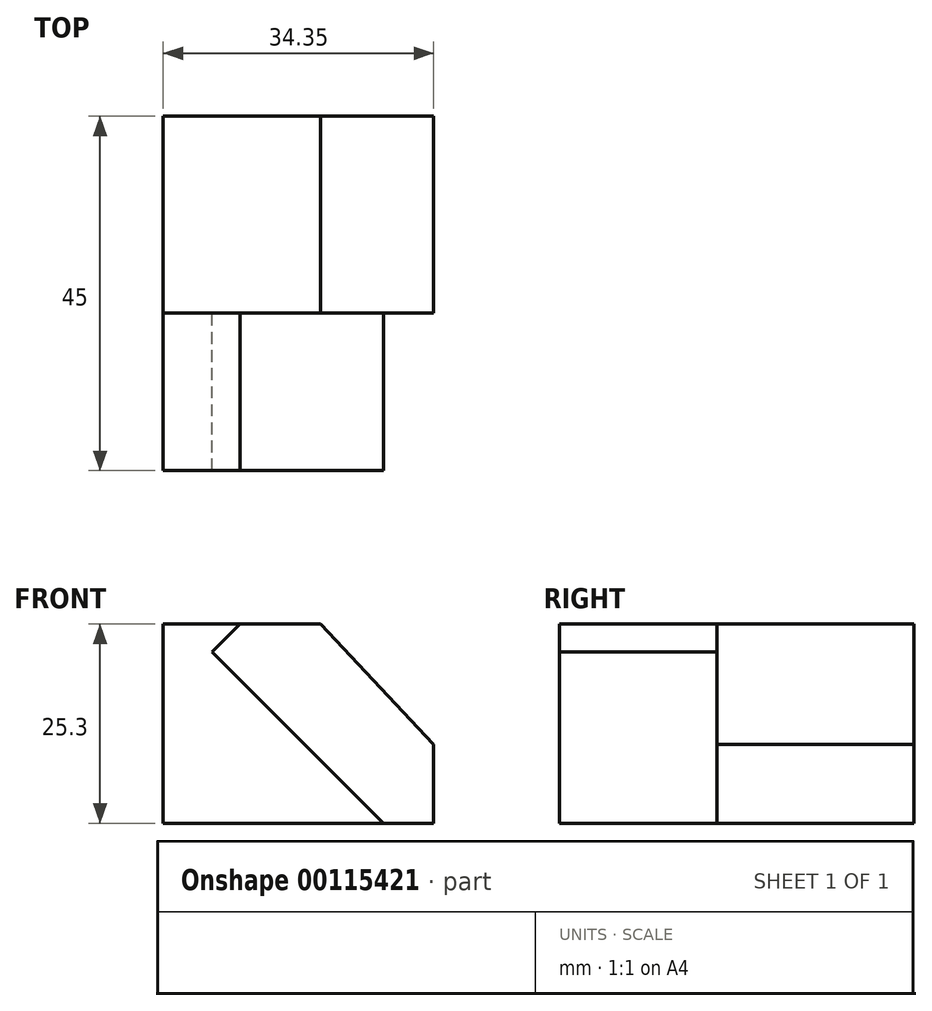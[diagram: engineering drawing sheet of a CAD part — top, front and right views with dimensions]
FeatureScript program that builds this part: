
annotation { "Feature Type Name" : "Feature", "Feature Type Description" : "" }
export const myFeature = defineFeature(function(context is Context, id is Id, definition is map)
    precondition{}
    {
        {
            var Q0;
            Q0=qCreatedBy(makeId("Front.planeOp"),FACE);
            var sketch = newSketch(context, id + "F0", { "sketchPlane" : qUnion([Q0])});
            skLineSegment(sketch, "E0", {"start": v(0, -6.35) * mm, "end": v(-28.11, 21.76) * mm, "construction": true});
            skLineSegment(sketch, "E1", {"start": v(0, 0) * mm, "end": v(-47.03, 0) * mm, "construction": true});
            skLineSegment(sketch, "E2", {"start": v(-6.35, 0) * mm, "end": v(-28.11, 21.76) * mm});
            skLineSegment(sketch, "E3", {"start": v(-28.11, 21.76) * mm, "end": v(-24.58, 25.3) * mm});
            skLineSegment(sketch, "E4", {"start": v(-24.58, 25.3) * mm, "end": v(-34.35, 25.3) * mm});
            skLineSegment(sketch, "E5", {"start": v(-34.35, 25.3) * mm, "end": v(-34.35, 0) * mm});
            skLineSegment(sketch, "E6", {"start": v(-34.35, 0) * mm, "end": v(-6.35, 0) * mm});
            skSolve(sketch);
        }
        {
            var Q0;
            Q0=makeQuery(id+"F0.imprint","IMPRINT",FACE,{"disambiguationData":[TD([[makeQuery(id+"F0.imprint","IMPRINT",EDGE,{"derivedFrom":sQuery(id+"F0.wireOp",EDGE,"E2")}),1.0]])]});
            extrude(context, id + "F1", {"entities" : qUnion([Q0]), "depth" : 20 * mm});
        }
        {
            var Q0;
            Q0=makeQuery(id+"F0.imprint","IMPRINT",FACE,{"disambiguationData":[TD([[makeQuery(id+"F0.imprint","IMPRINT",EDGE,{"derivedFrom":sQuery(id+"F0.wireOp",EDGE,"E2")}),1.0]])]});
            var sketch = newSketch(context, id + "F2", { "sketchPlane" : qUnion([Q0])});
            skLineSegment(sketch, "E7", {"start": v(-34.35, 0) * mm, "end": v(0, 0) * mm});
            skLineSegment(sketch, "E8", {"start": v(-34.35, 0) * mm, "end": v(-34.35, 25.3) * mm});
            skLineSegment(sketch, "E9", {"start": v(-34.35, 25.3) * mm, "end": v(-14.37, 25.3) * mm});
            skLineSegment(sketch, "E10", {"start": v(-14.37, 25.3) * mm, "end": v(0, 10) * mm});
            skLineSegment(sketch, "E11", {"start": v(0, 10) * mm, "end": v(0, 0) * mm});
            skPoint(sketch, "E12.1", {"position": v(-34.35, 25.3) * mm});
            skLineSegment(sketch, "E13.0", {"start": v(-24.58, 25.3) * mm, "end": v(-34.35, 25.3) * mm});
            skSolve(sketch);
        }
        {
            var Q0;
            Q0 = qSketchRegion(id + "F2", true);
            extrude(context, id + "F3", {"entities" : qUnion([Q0]), "oppositeDirection" : true, "depth" : 25 * mm});
        }
        {
            var Q0;
            Q0=makeQuery(id+"F1.opExtrude","SWEPT_FACE",FACE,{"disambiguationData":[OSD([sQuery(id+"F0.wireOp",EDGE,"E2")])]});
            var sketch = newSketch(context, id + "F4", { "sketchPlane" : qUnion([Q0])});
            skPoint(sketch, "E14", {"position": v(-20.27, -15) * mm});
            skSolve(sketch);
        }
        {
            var Q0;
            Q0=sQuery(id+"F4.wireOp",VERTEX,"E14");
            var Q1;
            Q1=makeQuery(id+"F1.opExtrude","SWEPT_BODY",BODY,{"disambiguationData":[OSD([sQuery(id+"F0.wireOp",EDGE,"E2"),sQuery(id+"F0.wireOp",EDGE,"E3"),sQuery(id+"F0.wireOp",EDGE,"E4"),sQuery(id+"F0.wireOp",EDGE,"E5"),sQuery(id+"F0.wireOp",EDGE,"E6")])]});
            hole(context, id + "F5", {"style" : HoleStyle.SIMPLE, "endStyle" : HoleEndStyle.THROUGH, "holeDiameter" : 2.7 * mm, "locations" : qUnion([Q0]), "scope" : qUnion([Q1]), "isTappedThrough" : true});
        }
    });
